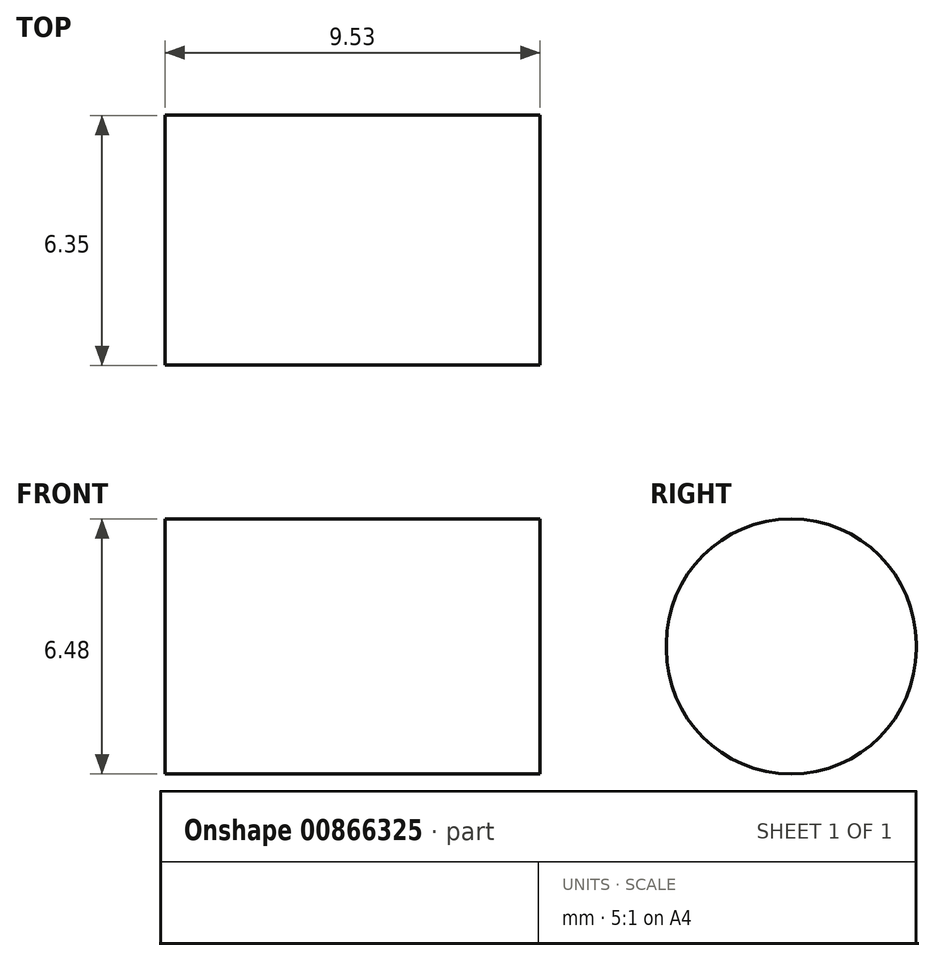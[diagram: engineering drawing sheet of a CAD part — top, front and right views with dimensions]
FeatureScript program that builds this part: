
annotation { "Feature Type Name" : "Feature", "Feature Type Description" : "" }
export const myFeature = defineFeature(function(context is Context, id is Id, definition is map)
    precondition{}
    {
        {
            var Q0;
            Q0=qCreatedBy(makeId("Right.planeOp"),FACE);
            var sketch = newSketch(context, id + "F0", { "sketchPlane" : qUnion([Q0])});
            skLineSegment(sketch, "E0.bottom", {"start": v(-22.23, 0) * mm, "end": v(22.23, 0) * mm});
            skLineSegment(sketch, "E0.top", {"start": v(-22.23, 50.8) * mm, "end": v(22.23, 50.8) * mm});
            skLineSegment(sketch, "E0.left", {"start": v(-22.23, 0) * mm, "end": v(-22.23, 50.8) * mm});
            skLineSegment(sketch, "E0.right", {"start": v(22.22, 0) * mm, "end": v(22.22, 50.8) * mm});
            skLineSegment(sketch, "E1", {"start": v(22.23, 50.8) * mm, "end": v(-22.23, 0) * mm, "construction": true});
            skSolve(sketch);
        }
        {
            var Q0;
            Q0=makeQuery(id+"F0.imprint","IMPRINT",FACE,{"disambiguationData":[TD([[makeQuery(id+"F0.imprint","IMPRINT",EDGE,{"derivedFrom":sQuery(id+"F0.wireOp",EDGE,"E0.bottom")}),1.0]])]});
            extrude(context, id + "F1", {"entities" : qUnion([Q0]), "endBound" : BoundingType.SYMMETRIC, "depth" : 314.32 * mm, "offsetDistance" : 25.4 * mm});
        }
        {
            var Q0;
            Q0=makeQuery(id+"F1.opExtrude","CAP_FACE",FACE,{"disambiguationData":[OSD([sQuery(id+"F0.wireOp",EDGE,"E0.bottom"),sQuery(id+"F0.wireOp",EDGE,"E0.top"),sQuery(id+"F0.wireOp",EDGE,"E0.left"),sQuery(id+"F0.wireOp",EDGE,"E0.right")])],"isStart":true});
            var sketch = newSketch(context, id + "F2", { "sketchPlane" : qUnion([Q0])});
            skLineSegment(sketch, "E2.bottom", {"start": v(22.23, 0) * mm, "end": v(-22.22, 0) * mm});
            skLineSegment(sketch, "E2.top", {"start": v(22.22, 279.4) * mm, "end": v(-22.23, 279.4) * mm});
            skLineSegment(sketch, "E2.left", {"start": v(22.23, 0) * mm, "end": v(22.22, 279.4) * mm});
            skLineSegment(sketch, "E2.right", {"start": v(-22.22, 0) * mm, "end": v(-22.23, 279.4) * mm});
            skSolve(sketch);
        }
        {
            var Q0;
            Q0=qSketchRegion(id+"F2",true);
            extrude(context, id + "F3", {"entities" : qUnion([Q0]), "depth" : 9.52 * mm, "offsetDistance" : 25.4 * mm});
        }
        {
            var Q0;
            Q0=makeQuery(id+"F3.opExtrude","SWEPT_EDGE",EDGE,{"disambiguationData":[OSD([sQuery(id+"F2.wireOp",EDGE,"E2.top"),sQuery(id+"F2.wireOp",EDGE,"E2.left")])]});
            var Q1;
            Q1=makeQuery(id+"F3.opExtrude","SWEPT_EDGE",EDGE,{"disambiguationData":[OSD([sQuery(id+"F2.wireOp",EDGE,"E2.top"),sQuery(id+"F2.wireOp",EDGE,"E2.right")])]});
            fillet(context, id + "F4", {"entities" : qUnion([Q0, Q1]), "radius" : 22.22 * mm, "tangentPropagation" : true, "allowEdgeOverflow" : false});
        }
        {
            var Q0;
            Q0=makeQuery(id+"F3.opExtrude","CAP_FACE",FACE,{"disambiguationData":[OSD([sQuery(id+"F2.wireOp",EDGE,"E2.bottom"),sQuery(id+"F2.wireOp",EDGE,"E2.top"),sQuery(id+"F2.wireOp",EDGE,"E2.left"),sQuery(id+"F2.wireOp",EDGE,"E2.right")])],"isStart":false});
            var sketch = newSketch(context, id + "F5", { "sketchPlane" : qUnion([Q0])});
            skPoint(sketch, "E3", {"position": v(0, 12.7) * mm});
            skPoint(sketch, "E4", {"position": v(0, 25.4) * mm});
            skPoint(sketch, "E5", {"position": v(0, 38.1) * mm});
            skPoint(sketch, "E6", {"position": v(0, 257.18) * mm});
            skPoint(sketch, "E7", {"position": v(0, 76.2) * mm});
            skLineSegment(sketch, "E8", {"start": v(0, 38.16) * mm, "end": v(0, 38.04) * mm});
            skArc(sketch, "E9.0.startCap", {"start": v(-3.18, 38.16) * mm, "mid": v(0, 41.34) * mm, "end": v(3.17, 38.16) * mm});
            skArc(sketch, "E9.0.endCap", {"start": v(3.17, 38.04) * mm, "mid": v(0, 34.86) * mm, "end": v(-3.18, 38.04) * mm});
            skLineSegment(sketch, "E9.0.left", {"start": v(3.17, 38.16) * mm, "end": v(3.17, 38.04) * mm});
            skLineSegment(sketch, "E9.0.right", {"start": v(-3.18, 38.16) * mm, "end": v(-3.18, 38.04) * mm});
            skSolve(sketch);
        }
        {
            var Q0;
            Q0=sQuery(id+"F5.wireOp",VERTEX,"E3");
            var Q1;
            Q1=makeQuery(id+"F3.opExtrude","SWEPT_BODY",BODY,{"disambiguationData":[OSD([sQuery(id+"F2.wireOp",EDGE,"E2.bottom"),sQuery(id+"F2.wireOp",EDGE,"E2.top"),sQuery(id+"F2.wireOp",EDGE,"E2.left"),sQuery(id+"F2.wireOp",EDGE,"E2.right")])]});
            hole(context, id + "F6", {"style" : HoleStyle.SIMPLE, "endStyle" : HoleEndStyle.THROUGH, "holeDiameter" : 6.53 * mm, "majorDiameter" : 6.35 * mm, "isTappedThrough" : true, "tappedDepth" : 12.7 * mm, "tapClearance" : 3, "locations" : qUnion([Q0]), "scope" : qUnion([Q1])});
        }
        {
            var Q0;
            Q0=sQuery(id+"F5.wireOp",VERTEX,"E4");
            var Q1;
            Q1=makeQuery(id+"F1.opExtrude","SWEPT_BODY",BODY,{"disambiguationData":[OSD([sQuery(id+"F0.wireOp",EDGE,"E0.bottom"),sQuery(id+"F0.wireOp",EDGE,"E0.top"),sQuery(id+"F0.wireOp",EDGE,"E0.left"),sQuery(id+"F0.wireOp",EDGE,"E0.right")])]});
            var Q2;
            Q2=makeQuery(id+"F3.opExtrude","SWEPT_BODY",BODY,{"disambiguationData":[OSD([sQuery(id+"F2.wireOp",EDGE,"E2.bottom"),sQuery(id+"F2.wireOp",EDGE,"E2.top"),sQuery(id+"F2.wireOp",EDGE,"E2.left"),sQuery(id+"F2.wireOp",EDGE,"E2.right")])]});
            hole(context, id + "F7", {"style" : HoleStyle.SIMPLE, "endStyle" : HoleEndStyle.BLIND_IN_LAST, "holeDiameter" : 6.53 * mm, "tapDrillDiameter" : 5.1 * mm, "majorDiameter" : 6.35 * mm, "holeDepth" : 16.5 * mm, "isTappedThrough" : true, "tappedDepth" : 12.7 * mm, "tapClearance" : 3, "locations" : qUnion([Q0]), "scope" : qUnion([Q1, Q2])});
        }
        {
            var Q0;
            Q0=sQuery(id+"F5.wireOp",VERTEX,"E6");
            var Q1;
            Q1=sQuery(id+"F5.wireOp",VERTEX,"E7");
            var Q2;
            Q2=makeQuery(id+"F3.opExtrude","SWEPT_BODY",BODY,{"disambiguationData":[OSD([sQuery(id+"F2.wireOp",EDGE,"E2.bottom"),sQuery(id+"F2.wireOp",EDGE,"E2.top"),sQuery(id+"F2.wireOp",EDGE,"E2.left"),sQuery(id+"F2.wireOp",EDGE,"E2.right")])]});
            hole(context, id + "F8", {"style" : HoleStyle.SIMPLE, "endStyle" : HoleEndStyle.THROUGH, "holeDiameter" : 15.88 * mm, "majorDiameter" : 6.35 * mm, "isTappedThrough" : true, "tappedDepth" : 12.7 * mm, "tapClearance" : 3, "locations" : qUnion([Q0, Q1]), "scope" : qUnion([Q2])});
        }
        {
            var Q0;
            Q0=qCreatedBy(makeId("Front.planeOp"),FACE);
            var sketch = newSketch(context, id + "F9", { "sketchPlane" : qUnion([Q0])});
            skLineSegment(sketch, "E10", {"start": v(-166.08, 87.31) * mm, "end": v(-166.08, 88.02) * mm});
            skLineSegment(sketch, "E11", {"start": v(-166.08, 88.02) * mm, "end": v(-164.9, 88.02) * mm});
            skLineSegment(sketch, "E12", {"start": v(-164.9, 88.02) * mm, "end": v(-164.9, 87.31) * mm});
            skLineSegment(sketch, "E13", {"start": v(-164.9, 87.31) * mm, "end": v(-158.43, 87.31) * mm});
            skLineSegment(sketch, "E14", {"start": v(-158.43, 87.31) * mm, "end": v(-158.43, 84.14) * mm});
            skLineSegment(sketch, "E15", {"start": v(-158.43, 84.14) * mm, "end": v(-157.16, 84.14) * mm});
            skLineSegment(sketch, "E16", {"start": v(-166.69, 76.2) * mm, "end": v(-150.9, 76.2) * mm, "construction": true});
            skLineSegment(sketch, "E17", {"start": v(-166.69, 84.14) * mm, "end": v(-166.69, 68.26) * mm, "construction": true});
            skLineSegment(sketch, "E18", {"start": v(-166.08, 87.31) * mm, "end": v(-166.69, 87.31) * mm});
            skLineSegment(sketch, "E19", {"start": v(-157.16, 76.2) * mm, "end": v(-157.16, 84.14) * mm});
            skLineSegment(sketch, "E20", {"start": v(-166.69, 76.2) * mm, "end": v(-157.16, 76.2) * mm});
            skLineSegment(sketch, "E21", {"start": v(-166.08, 268.29) * mm, "end": v(-166.08, 269) * mm});
            skLineSegment(sketch, "E22", {"start": v(-166.08, 269) * mm, "end": v(-164.9, 269) * mm});
            skLineSegment(sketch, "E23", {"start": v(-164.9, 269) * mm, "end": v(-164.9, 268.29) * mm});
            skLineSegment(sketch, "E24", {"start": v(-164.9, 268.29) * mm, "end": v(-158.43, 268.29) * mm});
            skLineSegment(sketch, "E25", {"start": v(-158.43, 268.29) * mm, "end": v(-158.43, 257.18) * mm});
            skLineSegment(sketch, "E26", {"start": v(-158.43, 257.18) * mm, "end": v(-157.16, 257.18) * mm});
            skLineSegment(sketch, "E27", {"start": v(-166.69, 257.18) * mm, "end": v(-157.16, 257.18) * mm, "construction": true});
            skLineSegment(sketch, "E28", {"start": v(-166.08, 268.29) * mm, "end": v(-166.69, 268.29) * mm});
            skLineSegment(sketch, "E29", {"start": v(-166.69, 268.29) * mm, "end": v(-166.69, 257.18) * mm});
            skLineSegment(sketch, "E30", {"start": v(-157.16, 257.18) * mm, "end": v(-157.16, 257.18) * mm});
            skLineSegment(sketch, "E31", {"start": v(-166.69, 257.18) * mm, "end": v(-157.16, 257.18) * mm});
            skLineSegment(sketch, "E32.0", {"start": v(-157.16, 265.11) * mm, "end": v(-157.16, 249.24) * mm, "construction": true});
            skLineSegment(sketch, "E33", {"start": v(-166.69, 87.31) * mm, "end": v(-166.69, 76.2) * mm});
            skSolve(sketch);
        }
        {
            var Q0;
            Q0=makeQuery(id+"F9.imprint","IMPRINT",FACE,{"disambiguationData":[TD([[makeQuery(id+"F9.imprint","IMPRINT",EDGE,{"derivedFrom":sQuery(id+"F9.wireOp",EDGE,"E10")}),-1.0]])]});
            var Q1;
            Q1=sQuery(id+"F9.wireOp",EDGE,"E16");
            revolve(context, id + "F10", {"operationType" : NewBodyOperationType.REMOVE, "surfaceOperationType" : NewSurfaceOperationType.NEW, "entities" : qUnion([Q0]), "axis" : qUnion([Q1]), "revolveType" : RevolveType.FULL, "oppositeDirection" : true});
        }
        {
            var Q0;
            Q0=makeQuery(id+"F9.imprint","IMPRINT",FACE,{"disambiguationData":[TD([[makeQuery(id+"F9.imprint","IMPRINT",EDGE,{"derivedFrom":sQuery(id+"F9.wireOp",EDGE,"E21")}),-1.0]])]});
            var Q1;
            Q1=sQuery(id+"F9.wireOp",EDGE,"E31");
            revolve(context, id + "F11", {"operationType" : NewBodyOperationType.REMOVE, "surfaceOperationType" : NewSurfaceOperationType.NEW, "entities" : qUnion([Q0]), "axis" : qUnion([Q1]), "revolveType" : RevolveType.FULL, "oppositeDirection" : true});
        }
        {
            var Q0;
            Q0=makeQuery(id+"F5.imprint","IMPRINT",FACE,{"disambiguationData":[TD([[makeQuery(id+"F5.imprint","IMPRINT",EDGE,{"derivedFrom":sQuery(id+"F5.wireOp",EDGE,"E9.0.startCap")}),-1.0]])]});
            extrude(context, id + "F12", {"entities" : qUnion([Q0]), "operationType" : NewBodyOperationType.REMOVE, "endBound" : BoundingType.THROUGH_ALL, "oppositeDirection" : true, "depth" : 25.4 * mm, "offsetDistance" : 25.4 * mm});
        }
        {
            var Q0;
            Q0=makeQuery(id+"F1.opExtrude","SWEPT_BODY",BODY,{"disambiguationData":[OSD([sQuery(id+"F0.wireOp",EDGE,"E0.bottom"),sQuery(id+"F0.wireOp",EDGE,"E0.top"),sQuery(id+"F0.wireOp",EDGE,"E0.left"),sQuery(id+"F0.wireOp",EDGE,"E0.right")])]});
            deleteBodies(context, id + "F13", {"entities" : qUnion([Q0])});
        }
    });
